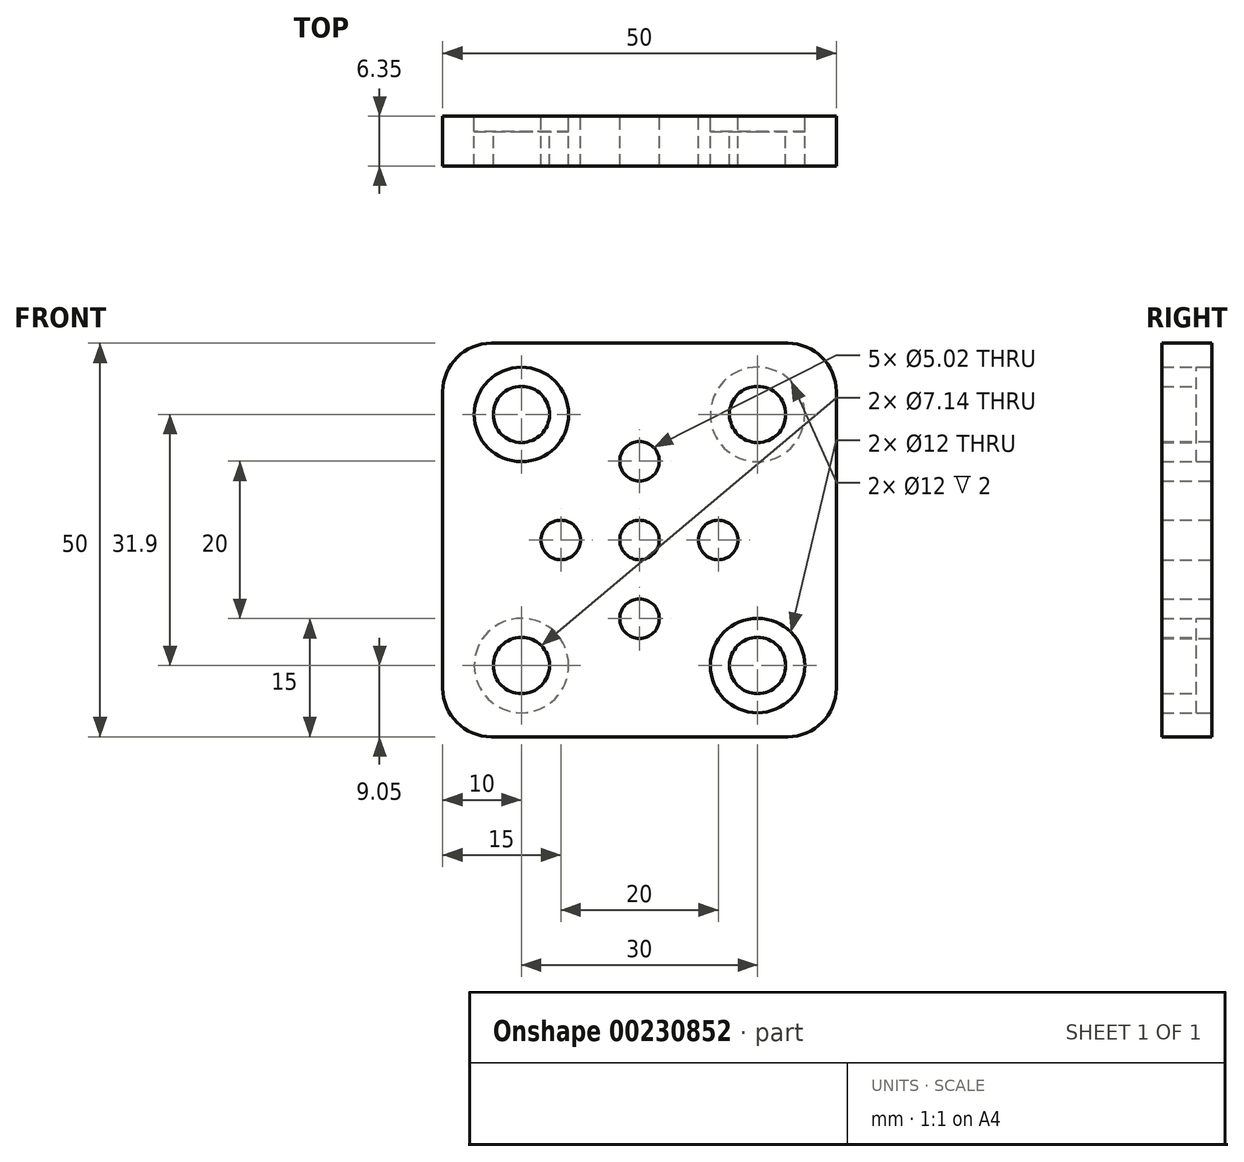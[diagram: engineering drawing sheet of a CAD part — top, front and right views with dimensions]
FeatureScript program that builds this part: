
annotation { "Feature Type Name" : "Feature", "Feature Type Description" : "" }
export const myFeature = defineFeature(function(context is Context, id is Id, definition is map)
    precondition{}
    {
        {
            var Q0;
            Q0=qCreatedBy(makeId("Front.planeOp"),FACE);
            var sketch = newSketch(context, id + "F0", { "sketchPlane" : qUnion([Q0])});
            skLineSegment(sketch, "E0.bottom", {"start": v(18.83, -25) * mm, "end": v(-18.83, -25) * mm});
            skLineSegment(sketch, "E0.top", {"start": v(18.83, 25) * mm, "end": v(-18.83, 25) * mm});
            skLineSegment(sketch, "E0.left", {"start": v(25, -18.83) * mm, "end": v(25, 18.83) * mm});
            skLineSegment(sketch, "E0.right", {"start": v(-25, -18.83) * mm, "end": v(-25, 18.83) * mm});
            skPoint(sketch, "E0.middle", {"position": v(0, 0) * mm});
            skPoint(sketch, "E1.visualSharp", {"position": v(-25, 25) * mm});
            skArc(sketch, "E1.filletArc", {"start": v(-18.83, 25) * mm, "mid": v(-23.2, 23.2) * mm, "end": v(-25, 18.83) * mm});
            skPoint(sketch, "E2.visualSharp", {"position": v(25, 25) * mm});
            skArc(sketch, "E2.filletArc", {"start": v(25, 18.83) * mm, "mid": v(23.2, 23.2) * mm, "end": v(18.83, 25) * mm});
            skPoint(sketch, "E3.visualSharp", {"position": v(25, -25) * mm});
            skArc(sketch, "E3.filletArc", {"start": v(18.83, -25) * mm, "mid": v(23.2, -23.2) * mm, "end": v(25, -18.83) * mm});
            skPoint(sketch, "E4.visualSharp", {"position": v(-25, -25) * mm});
            skArc(sketch, "E4.filletArc", {"start": v(-25, -18.83) * mm, "mid": v(-23.2, -23.2) * mm, "end": v(-18.83, -25) * mm});
            skLineSegment(sketch, "E5", {"start": v(0, -8.7) * mm, "end": v(0, -8.7) * mm});
            skPoint(sketch, "E5.startSnap0", {"position": v(0, 25) * mm});
            skPoint(sketch, "E5.endSnap0", {"position": v(0, -25) * mm});
            skLineSegment(sketch, "E6", {"start": v(-29.16, 0) * mm, "end": v(28.42, 0) * mm, "construction": true});
            skPoint(sketch, "E6.startSnap0", {"position": v(-25, 0) * mm});
            skCircle(sketch, "E7", {"center": v(15, 15.95) * mm, "radius": 3.57 * mm});
            skCircle(sketch, "E8.0", {"center": v(15, 15.95) * mm, "radius": 6 * mm});
            skCircle(sketch, "E9.MirrorC", {"center": v(15, -15.95) * mm, "radius": 3.57 * mm});
            skCircle(sketch, "E10.MirrorC", {"center": v(15, -15.95) * mm, "radius": 6 * mm});
            skCircle(sketch, "E11.MirrorC", {"center": v(-15, -15.95) * mm, "radius": 3.57 * mm});
            skCircle(sketch, "E12.MirrorC", {"center": v(-15, -15.95) * mm, "radius": 6 * mm});
            skCircle(sketch, "E13.MirrorC", {"center": v(-15, 15.95) * mm, "radius": 3.57 * mm});
            skCircle(sketch, "E14.MirrorC", {"center": v(-15, 15.95) * mm, "radius": 6 * mm});
            skCircle(sketch, "E15", {"center": v(0, 0) * mm, "radius": 2.5 * mm});
            skCircle(sketch, "E16", {"center": v(0, -10) * mm, "radius": 2.5 * mm});
            skCircle(sketch, "E17", {"center": v(0, 10) * mm, "radius": 2.5 * mm});
            skCircle(sketch, "E18", {"center": v(-10, 0) * mm, "radius": 2.5 * mm});
            skCircle(sketch, "E19", {"center": v(10, 0) * mm, "radius": 2.5 * mm});
            skSolve(sketch);
        }
        {
            var Q0;
            Q0=makeQuery(id+"F0.imprint","IMPRINT",FACE,{"disambiguationData":[TD([[makeQuery(id+"F0.imprint","IMPRINT",EDGE,{"derivedFrom":sQuery(id+"F0.wireOp",EDGE,"E0.bottom")}),-1.0]])]});
            var Q1;
            Q1=makeQuery(id+"F0.imprint","IMPRINT",FACE,{"disambiguationData":[TD([[makeQuery(id+"F0.imprint","IMPRINT",EDGE,{"derivedFrom":sQuery(id+"F0.wireOp",EDGE,"E13.MirrorC")}),1.0]])]});
            var Q2;
            Q2=makeQuery(id+"F0.imprint","IMPRINT",FACE,{"disambiguationData":[TD([[makeQuery(id+"F0.imprint","IMPRINT",EDGE,{"derivedFrom":sQuery(id+"F0.wireOp",EDGE,"E7")}),-1.0]])]});
            var Q3;
            Q3=makeQuery(id+"F0.imprint","IMPRINT",FACE,{"disambiguationData":[TD([[makeQuery(id+"F0.imprint","IMPRINT",EDGE,{"derivedFrom":sQuery(id+"F0.wireOp",EDGE,"E9.MirrorC")}),1.0]])]});
            var Q4;
            Q4=makeQuery(id+"F0.imprint","IMPRINT",FACE,{"disambiguationData":[TD([[makeQuery(id+"F0.imprint","IMPRINT",EDGE,{"derivedFrom":sQuery(id+"F0.wireOp",EDGE,"E11.MirrorC")}),-1.0]])]});
            extrude(context, id + "F1", {"entities" : qUnion([Q0, Q1, Q2, Q3, Q4]), "depth" : 6.35 * mm});
        }
        {
            var Q0;
            Q0=makeQuery(id+"F0.imprint","IMPRINT",FACE,{"disambiguationData":[TD([[makeQuery(id+"F0.imprint","IMPRINT",EDGE,{"derivedFrom":sQuery(id+"F0.wireOp",EDGE,"E7")}),-1.0]])]});
            var Q1;
            Q1=makeQuery(id+"F0.imprint","IMPRINT",FACE,{"disambiguationData":[TD([[makeQuery(id+"F0.imprint","IMPRINT",EDGE,{"derivedFrom":sQuery(id+"F0.wireOp",EDGE,"E13.MirrorC")}),1.0]])]});
            var Q2;
            Q2=makeQuery(id+"F0.imprint","IMPRINT",FACE,{"disambiguationData":[TD([[makeQuery(id+"F0.imprint","IMPRINT",EDGE,{"derivedFrom":sQuery(id+"F0.wireOp",EDGE,"E11.MirrorC")}),-1.0]])]});
            var Q3;
            Q3=makeQuery(id+"F0.imprint","IMPRINT",FACE,{"disambiguationData":[TD([[makeQuery(id+"F0.imprint","IMPRINT",EDGE,{"derivedFrom":sQuery(id+"F0.wireOp",EDGE,"E9.MirrorC")}),1.0]])]});
            extrude(context, id + "F2", {"entities" : qUnion([Q0, Q1, Q2, Q3]), "operationType" : NewBodyOperationType.REMOVE, "depth" : 2 * mm});
        }
    });
